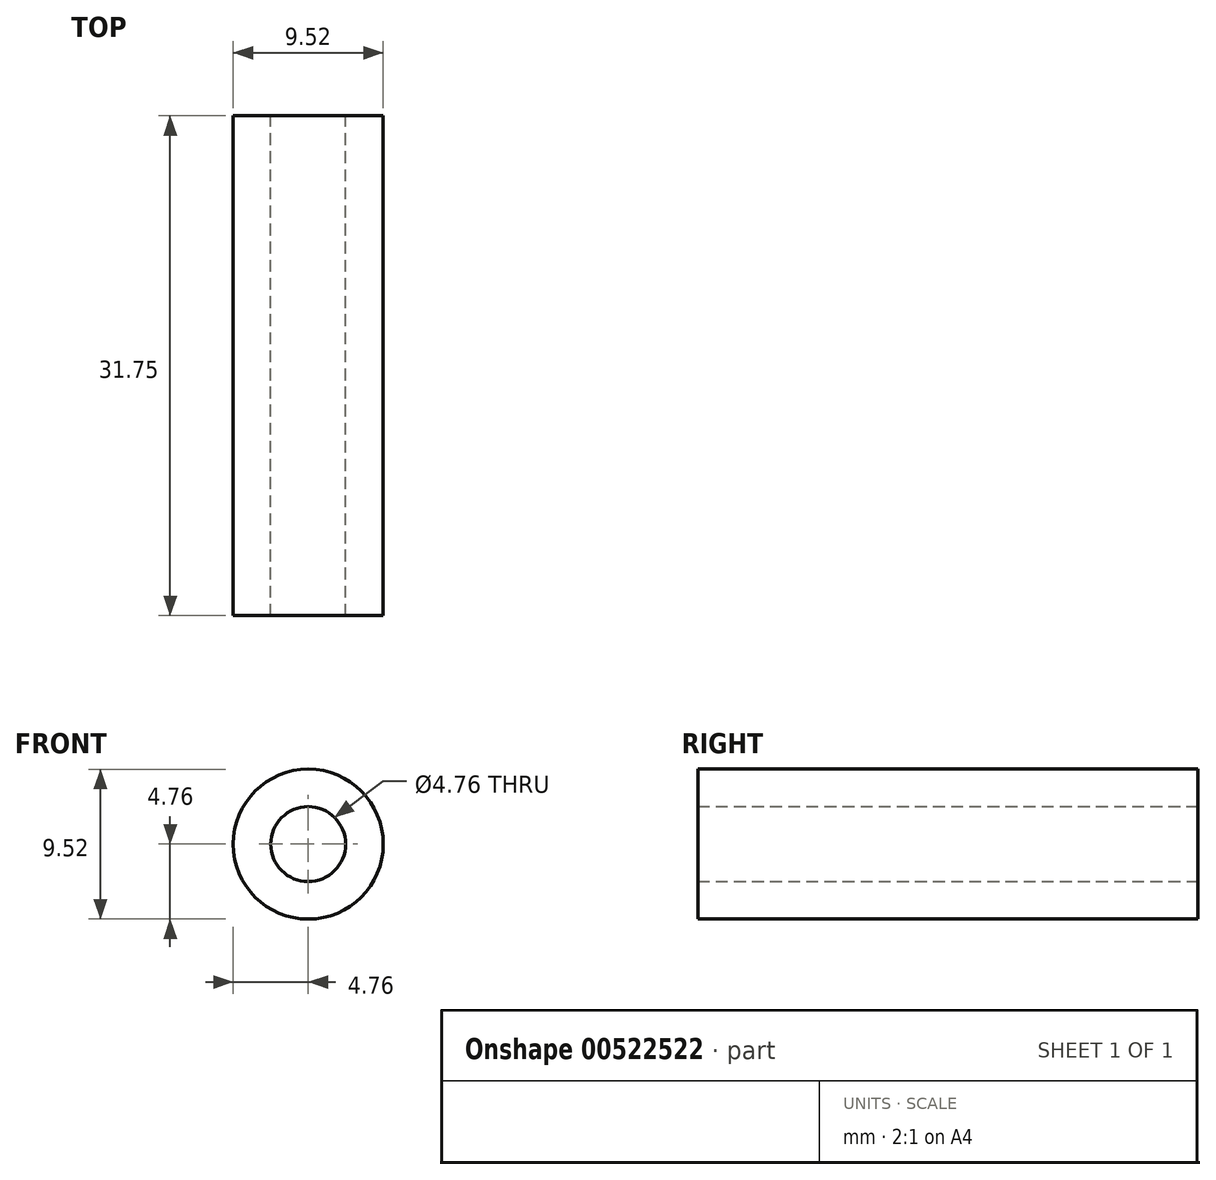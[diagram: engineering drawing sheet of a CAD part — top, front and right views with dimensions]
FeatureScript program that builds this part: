
annotation { "Feature Type Name" : "Feature", "Feature Type Description" : "" }
export const myFeature = defineFeature(function(context is Context, id is Id, definition is map)
    precondition{}
    {
        {
            assignVariable(context, id + "F0", {"name" : "thickness", "lengthValue" : 31.75 * mm, "minmax" : VariableMinMaxSelection.MINIMUM, "extendEntities" : false, "measureFromAxis" : false, "distance" : 0 * mm, "xOffset" : 0 * mm, "yOffset" : 0 * mm, "zOffset" : 0 * mm, "componentSelector" : AxisWithCustom.DISTANCE, "customOffset" : 0 * mm, "radius" : false, "description" : "", "variableType" : VariableType.LENGTH, "measurementMode" : VariableMeasurementMode.DISTANCE, "mode" : VariableMode.ASSIGNED});
        }
        {
            var Q0;
            Q0=qCreatedBy(makeId("Front.planeOp"),FACE);
            var sketch = newSketch(context, id + "F1", { "sketchPlane" : qUnion([Q0]), "disableImprinting" : false});
            skCircle(sketch, "E0", {"center": v(0, 0) * mm, "radius": 2.38 * mm});
            skCircle(sketch, "E1", {"center": v(0, 0) * mm, "radius": 4.76 * mm});
            skSolve(sketch);
        }
        {
            var Q0;
            Q0=makeQuery(id+"F1.imprint","IMPRINT",FACE,{"disambiguationData":[TD([[makeQuery(id+"F1.imprint","IMPRINT",EDGE,{"derivedFrom":sQuery(id+"F1.wireOp",EDGE,"E0")}),-1.0]])]});
            extrude(context, id + "F2", {"entities" : qUnion([Q0]), "flatOperationType" : FlatOperationType.REMOVE, "thickness1" : 5 * mm, "thickness2" : 0 * mm, "thickness" : 5 * mm, "depth" : (getVariable(context, 'thickness')), "offsetDistance" : 25 * mm, "startOffsetBound" : StartOffsetType.BLIND, "startOffsetDistance" : 25 * mm, "domain" : OperationDomain.MODEL});
        }
    });
